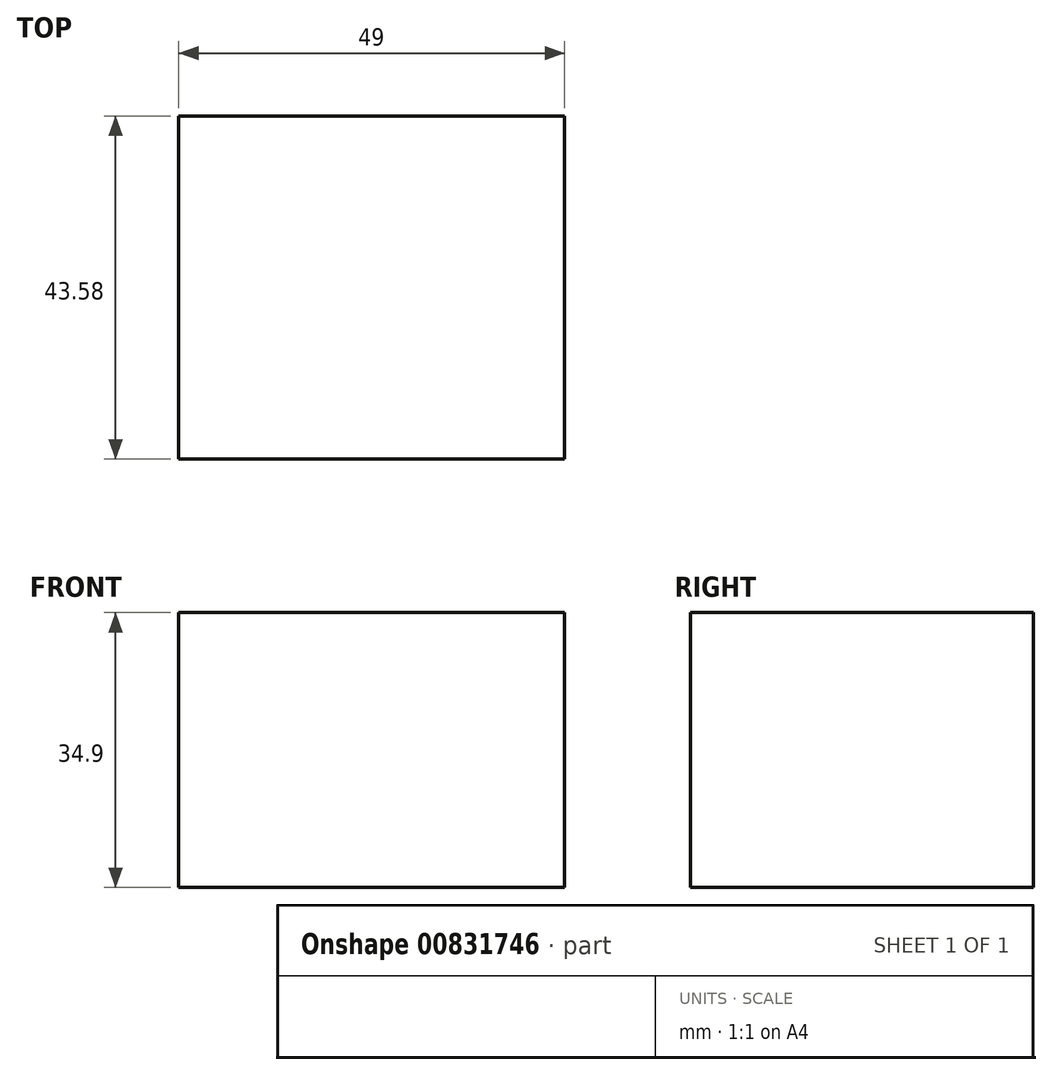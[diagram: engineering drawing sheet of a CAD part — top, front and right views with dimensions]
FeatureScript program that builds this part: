
annotation { "Feature Type Name" : "Feature", "Feature Type Description" : "" }
export const myFeature = defineFeature(function(context is Context, id is Id, definition is map)
    precondition{}
    {
        {
            var Q0;
            Q0=qCreatedBy(makeId("Top.planeOp"),FACE);
            var sketch = newSketch(context, id + "F0", { "sketchPlane" : qUnion([Q0])});
            skLineSegment(sketch, "E0.bottom", {"start": v(-24.5, 21.8) * mm, "end": v(24.5, 21.8) * mm});
            skLineSegment(sketch, "E0.top", {"start": v(-24.5, -21.8) * mm, "end": v(24.5, -21.8) * mm});
            skLineSegment(sketch, "E0.left", {"start": v(-24.5, 21.8) * mm, "end": v(-24.5, -21.8) * mm});
            skLineSegment(sketch, "E0.right", {"start": v(24.5, 21.8) * mm, "end": v(24.5, -21.8) * mm});
            skPoint(sketch, "E0.middle", {"position": v(0, 0) * mm});
            skSolve(sketch);
        }
        {
            var Q0;
            Q0=makeQuery(id+"F0.imprint","IMPRINT",FACE,{"disambiguationData":[TD([[makeQuery(id+"F0.imprint","IMPRINT",EDGE,{"derivedFrom":sQuery(id+"F0.wireOp",EDGE,"E0.bottom")}),-1.0]])]});
            extrude(context, id + "F1", {"entities" : qUnion([Q0]), "depth" : 34.9 * mm, "offsetDistance" : 25 * mm});
        }
    });
